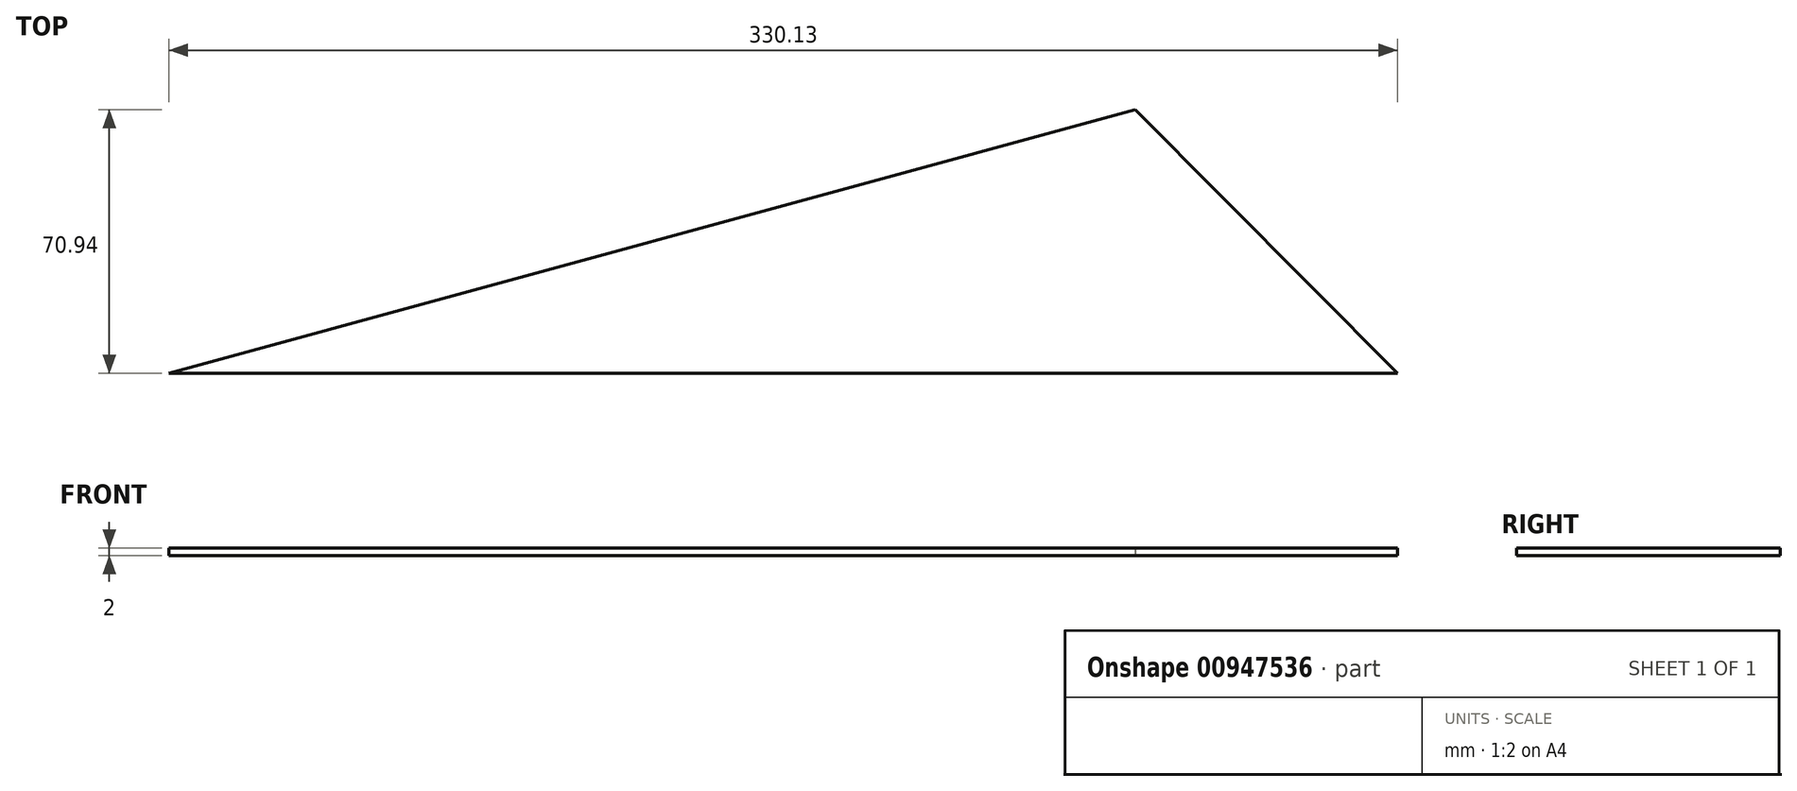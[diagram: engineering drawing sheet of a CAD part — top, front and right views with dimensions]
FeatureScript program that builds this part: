
annotation { "Feature Type Name" : "Feature", "Feature Type Description" : "" }
export const myFeature = defineFeature(function(context is Context, id is Id, definition is map)
    precondition{}
    {
        {
            var Q0;
            Q0=qCreatedBy(makeId("Top.planeOp"),FACE);
            var sketch = newSketch(context, id + "F0", { "sketchPlane" : qUnion([Q0])});
            skLineSegment(sketch, "E0", {"start": v(-137.78, -16.9) * mm, "end": v(121.87, 54.04) * mm});
            skLineSegment(sketch, "E1", {"start": v(121.87, 54.04) * mm, "end": v(192.35, -16.9) * mm});
            skLineSegment(sketch, "E2", {"start": v(192.35, -16.9) * mm, "end": v(-137.78, -16.9) * mm});
            skSolve(sketch);
        }
        {
            var Q0;
            Q0 = qSketchRegion(id + "F0", true);
            extrude(context, id + "F1", {"entities" : qUnion([Q0]), "depth" : 2 * mm, "offsetDistance" : 25 * mm});
        }
    });
